# Revit family: IEK_Держатель проводника круглого_6-8мм_Черепичная кровля_Оцинкованная сталь
name_source: partatom
category: Обобщенные модели
units: mm (PartAtom-declared; Revit-internal decimal feet)

## family parameters
Может служить основой для арматурных стержней = Нет
Общий = Да
Основа = Грань
При загрузке вырезать с полостями = Нет
Размер круглого соединителя = Использовать диаметр
Тип детали = Нормальный
Точка расчета площади = Нет

## types (2) — shared parameters
ADSK_URL страницы изделия = https://www.iek.ru
ADSK_Версия Revit = 2019
ADSK_Версия семейства = 1.0
ADSK_Группирование = VIII. ЭЛЕМЕНТЫ ВНЕШНЕЙ МОЛНИЕЗАЩИТЫ
ADSK_Единица измерения = шт
ADSK_Завод-изготовитель = IEK
IEK_Описание = Универсальная конструкция держателя позволяет использовать его с проводниками различной формы и габаритами.
Длина = 360 мм
Ширина = 24 мм
zero-valued in all types: Отметка по умолчанию

## per-type parameters (varying)
| type | ADSK_Код изделия | ADSK_Масса | ADSK_Материал | ADSK_Материал наименование | ADSK_Наименование | IEK_URL | IEK_Цена за единицу | KSI_CMa_Строительные материалы |
| 6-8_Сталь оцникованная | ZDP80-11-5-68 | 0.085 | Сталь оцинкованная | Сталь оцинкованная | Дер. пров. кругл. 6-8мм черепичная кровля оц. сталь IEK | https://www.iek.ru | 350 | 24.10.35.000.08.3.05.06-0001 |
| 6-8_Медь | ZDP80-50-5-68 | 0.09 | Медь | Медь | Дер. пров. кругл. 6-8мм черепичная кровля медь IEK |  | 704 | СТ 10 12 20 10 |
